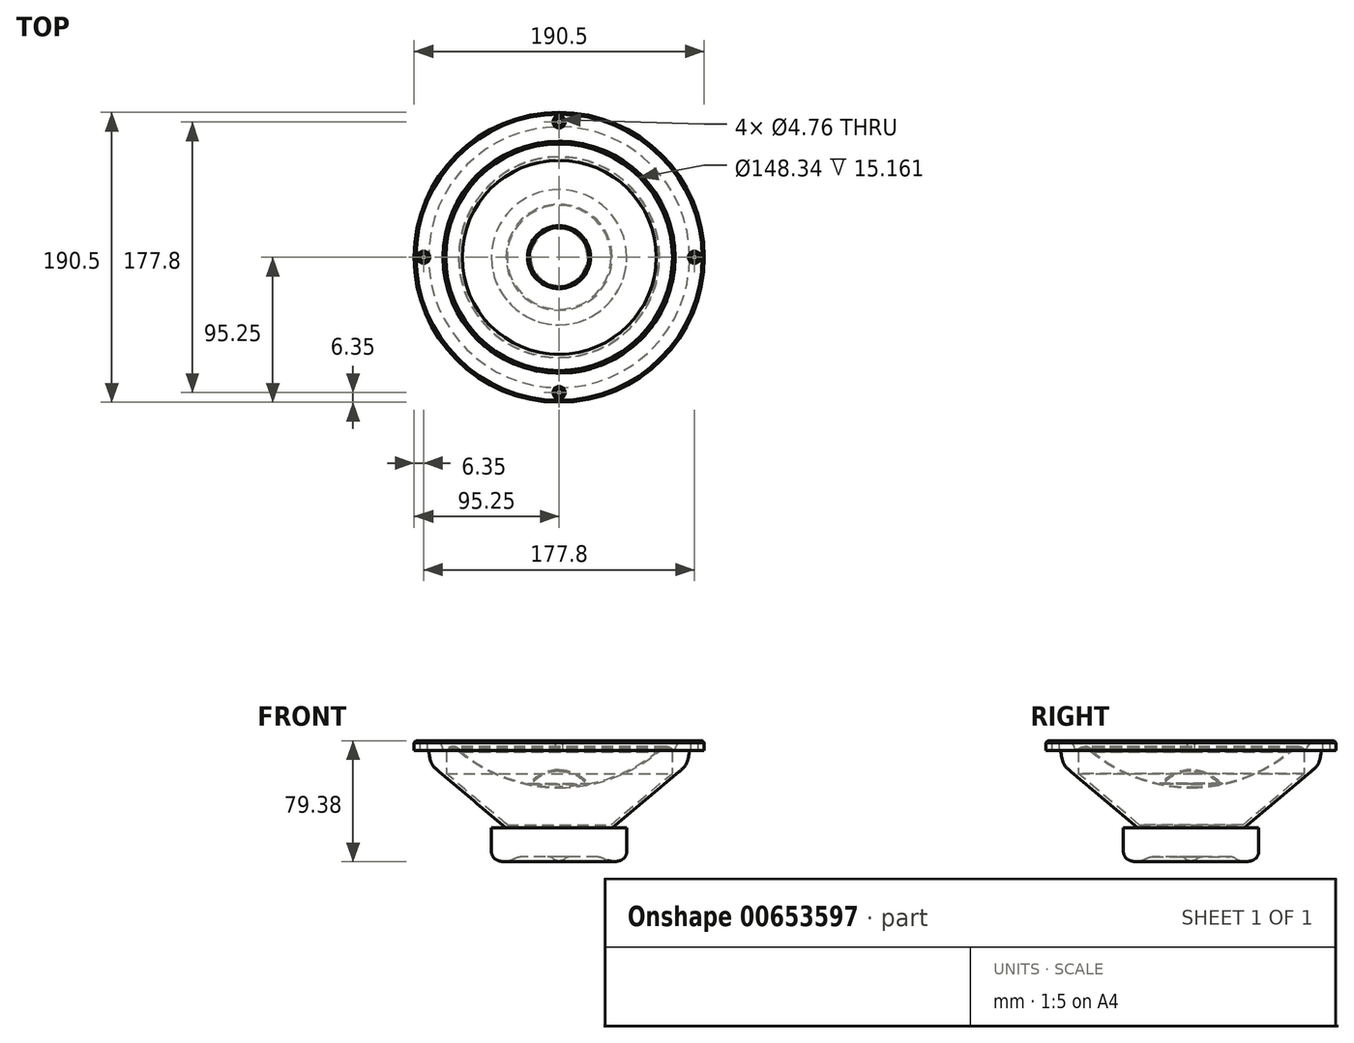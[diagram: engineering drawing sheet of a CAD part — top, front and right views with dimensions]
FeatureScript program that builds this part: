
annotation { "Feature Type Name" : "Feature", "Feature Type Description" : "" }
export const myFeature = defineFeature(function(context is Context, id is Id, definition is map)
    precondition{}
    {
        {
            var Q0;
            Q0=qCreatedBy(makeId("Front.planeOp"),FACE);
            var sketch = newSketch(context, id + "F0", { "sketchPlane" : qUnion([Q0])});
            skLineSegment(sketch, "E0", {"start": v(95.25, 76.2) * mm, "end": v(95.25, 69.85) * mm});
            skLineSegment(sketch, "E1", {"start": v(95.25, 69.85) * mm, "end": v(85.72, 69.85) * mm});
            skLineSegment(sketch, "E2", {"start": v(44.45, 19.05) * mm, "end": v(44.45, 0) * mm});
            skLineSegment(sketch, "E3", {"start": v(27.65, 0) * mm, "end": v(5.08, 0) * mm});
            skLineSegment(sketch, "E4", {"start": v(0, 0) * mm, "end": v(0, 76.2) * mm});
            skLineSegment(sketch, "E5", {"start": v(0, 0) * mm, "end": v(0, 96.52) * mm, "construction": true});
            skLineSegment(sketch, "E6", {"start": v(85.72, 69.85) * mm, "end": v(84.05, 60.33) * mm});
            skLineSegment(sketch, "E7", {"start": v(84.05, 60.33) * mm, "end": v(34.86, 19.05) * mm});
            skLineSegment(sketch, "E8", {"start": v(34.86, 19.05) * mm, "end": v(44.45, 19.05) * mm});
            skLineSegment(sketch, "E9", {"start": v(85.72, 69.85) * mm, "end": v(85.72, 49.69) * mm, "construction": true});
            skLineSegment(sketch, "E10", {"start": v(95.25, 76.2) * mm, "end": v(76.2, 76.2) * mm});
            skArc(sketch, "E11", {"start": v(19.5, 48.04) * mm, "mid": v(10.76, 54.76) * mm, "end": v(0, 57.15) * mm});
            skLineSegment(sketch, "E12", {"start": v(76.2, 76.2) * mm, "end": v(76.2, 69.85) * mm});
            skPoint(sketch, "E13.orphan", {"position": v(-19.67, 47.81) * mm});
            skArc(sketch, "E14.trimOffspring", {"start": v(19.67, 47.81) * mm, "mid": v(44.13, 55.98) * mm, "end": v(65.75, 70.03) * mm});
            skPoint(sketch, "E15.center.orphan", {"position": v(0, 148.62) * mm});
            skPoint(sketch, "E15.start.orphan", {"position": v(-65.75, 70.03) * mm});
            skArc(sketch, "E16", {"start": v(-65.75, 70.03) * mm, "mid": v(-35.02, 52.12) * mm, "end": v(0, 45.9) * mm, "construction": true});
            skArc(sketch, "E17", {"start": v(0, 57.15) * mm, "mid": v(-10.89, 54.7) * mm, "end": v(-19.67, 47.81) * mm, "construction": true});
            skArc(sketch, "E18", {"start": v(0, 45.38) * mm, "mid": v(35.2, 51.64) * mm, "end": v(66.07, 69.64) * mm});
            skArc(sketch, "E19", {"start": v(19.67, 47.81) * mm, "mid": v(9.88, 46.37) * mm, "end": v(0, 45.9) * mm});
            skArc(sketch, "E20", {"start": v(18.53, 47.6) * mm, "mid": v(10.2, 53.9) * mm, "end": v(0, 56.13) * mm});
            skArc(sketch, "E21", {"start": v(19.5, 48.04) * mm, "mid": v(20.06, 48.15) * mm, "end": v(20.64, 48.27) * mm});
            skLineSegment(sketch, "E22", {"start": v(20.64, 48.27) * mm, "end": v(20.69, 48.02) * mm});
            skLineSegment(sketch, "E23", {"start": v(34.86, 19.05) * mm, "end": v(0, 19.05) * mm});
            skLineSegment(sketch, "E24", {"start": v(74.17, 54.69) * mm, "end": v(34.12, 21.08) * mm});
            skLineSegment(sketch, "E25", {"start": v(34.12, 21.08) * mm, "end": v(0, 21.08) * mm});
            skLineSegment(sketch, "E26", {"start": v(76.2, 69.85) * mm, "end": v(74.17, 69.85) * mm});
            skLineSegment(sketch, "E27", {"start": v(74.17, 69.85) * mm, "end": v(74.17, 54.69) * mm});
            skLineSegment(sketch, "E28", {"start": v(74.46, 70.61) * mm, "end": v(76.2, 70.61) * mm});
            skLineSegment(sketch, "E29", {"start": v(65.75, 70.03) * mm, "end": v(66.07, 69.64) * mm});
            skArc(sketch, "E30", {"start": v(74.46, 70.61) * mm, "mid": v(69.85, 72.3) * mm, "end": v(65.25, 70.61) * mm});
            skArc(sketch, "E31", {"start": v(74.17, 69.85) * mm, "mid": v(70, 71.54) * mm, "end": v(65.75, 70.03) * mm});
            skArc(sketch, "E32", {"start": v(63.7, 69.31) * mm, "mid": v(64.47, 69.96) * mm, "end": v(65.25, 70.61) * mm});
            skLineSegment(sketch, "E33", {"start": v(63.7, 69.31) * mm, "end": v(64.17, 68.72) * mm});
            skArc(sketch, "E34", {"start": v(27.65, 0) * mm, "mid": v(36.05, -3.17) * mm, "end": v(44.45, 0) * mm});
            skArc(sketch, "E35", {"start": v(0, -2.54) * mm, "mid": v(2.84, -1.87) * mm, "end": v(5.08, 0) * mm});
            skLineSegment(sketch, "E36", {"start": v(0, 0) * mm, "end": v(0, -2.54) * mm});
            skSolve(sketch);
        }
        {
            var Q0;
            Q0=makeQuery(id+"F0.imprint","IMPRINT",FACE,{"disambiguationData":[TD([[makeQuery(id+"F0.imprint","IMPRINT",EDGE,{"derivedFrom":sQuery(id+"F0.wireOp",EDGE,"E0")}),-1.0]])]});
            var Q1;
            Q1=sQuery(id+"F0.wireOp",EDGE,"E5");
            revolve(context, id + "F1", {"entities" : qUnion([Q0]), "axis" : qUnion([Q1]), "revolveType" : RevolveType.FULL});
        }
        {
            var Q0;
            {var subQ0=sQuery(id+"F0.wireOp",EDGE,"E26");Q0=makeQuery(id+"F0.imprint","IMPRINT",FACE,{"disambiguationData":[TD([[makeQuery(id+"F0.imprint","IMPRINT",EDGE,{"derivedFrom":subQ0}),-1.0]])]});}
            var Q1;
            Q1=sQuery(id+"F0.wireOp",EDGE,"E5");
            revolve(context, id + "F2", {"entities" : qUnion([Q0]), "axis" : qUnion([Q1]), "revolveType" : RevolveType.FULL});
        }
        {
            var Q0;
            {var subQ0=sQuery(id+"F0.wireOp",EDGE,"E18");Q0=makeQuery(id+"F0.imprint","IMPRINT",FACE,{"disambiguationData":[TD([[makeQuery(id+"F0.imprint","IMPRINT",EDGE,{"derivedFrom":subQ0}),1.0]])]});}
            var Q1;
            Q1=sQuery(id+"F0.wireOp",EDGE,"E5");
            revolve(context, id + "F3", {"entities" : qUnion([Q0]), "axis" : qUnion([Q1]), "revolveType" : RevolveType.FULL});
        }
        {
            var Q0;
            {var subQ5=sQuery(id+"F0.wireOp",EDGE,"E11");Q0=makeQuery(id+"F0.imprint","IMPRINT",FACE,{"disambiguationData":[TD([[makeQuery(id+"F0.imprint","IMPRINT",EDGE,{"derivedFrom":subQ5}),1.0]])]});}
            var Q1;
            Q1=sQuery(id+"F0.wireOp",EDGE,"E5");
            revolve(context, id + "F4", {"entities" : qUnion([Q0]), "axis" : qUnion([Q1]), "revolveType" : RevolveType.FULL});
        }
        {
            var Q0;
            Q0=makeQuery(id+"F0.imprint","IMPRINT",FACE,{"disambiguationData":[TD([[makeQuery(id+"F0.imprint","IMPRINT",EDGE,{"derivedFrom":sQuery(id+"F0.wireOp",EDGE,"E2")}),-1.0]])]});
            var Q1;
            Q1=sQuery(id+"F0.wireOp",EDGE,"E5");
            revolve(context, id + "F5", {"entities" : qUnion([Q0]), "axis" : qUnion([Q1]), "revolveType" : RevolveType.FULL});
        }
        {
            var Q0;
            Q0=makeQuery(id+"F1.opRevolve","SWEPT_FACE",FACE,{"disambiguationData":[OSD([sQuery(id+"F0.wireOp",EDGE,"E10")])]});
            var sketch = newSketch(context, id + "F6", { "sketchPlane" : qUnion([Q0])});
            skCircle(sketch, "E37", {"center": v(0, 0) * mm, "radius": 88.9 * mm, "construction": true});
            skPoint(sketch, "E38", {"position": v(0, 88.9) * mm});
            skPoint(sketch, "E39", {"position": v(88.9, 0) * mm});
            skPoint(sketch, "E40", {"position": v(0, -88.9) * mm});
            skPoint(sketch, "E41", {"position": v(-88.9, 0) * mm});
            skSolve(sketch);
        }
        {
            var Q0;
            Q0=sQuery(id+"F6.wireOp",VERTEX,"E38");
            var Q1;
            Q1=sQuery(id+"F6.wireOp",VERTEX,"E39");
            var Q2;
            Q2=sQuery(id+"F6.wireOp",VERTEX,"E40");
            var Q3;
            Q3=sQuery(id+"F6.wireOp",VERTEX,"E41");
            var Q4;
            Q4=makeQuery(id+"F1.opRevolve","SWEPT_BODY",BODY,{"disambiguationData":[OSD([sQuery(id+"F0.wireOp",EDGE,"E0"),sQuery(id+"F0.wireOp",EDGE,"E1"),sQuery(id+"F0.wireOp",EDGE,"E2"),sQuery(id+"F0.wireOp",EDGE,"E3"),sQuery(id+"F0.wireOp",EDGE,"E4"),sQuery(id+"F0.wireOp",EDGE,"E6"),sQuery(id+"F0.wireOp",EDGE,"E7"),sQuery(id+"F0.wireOp",EDGE,"E8"),sQuery(id+"F0.wireOp",EDGE,"E10"),sQuery(id+"F0.wireOp",EDGE,"E11"),sQuery(id+"F0.wireOp",EDGE,"E12"),sQuery(id+"F0.wireOp",EDGE,"oivfGs8H-isbq-zMFm-OgCN-3ZXWerDyivmW"),sQuery(id+"F0.wireOp",EDGE,"E14.trimOffspring")])]});
            hole(context, id + "F7", {"style" : HoleStyle.C_SINK, "endStyle" : HoleEndStyle.THROUGH, "holeDiameter" : 4.76 * mm, "cSinkDiameter" : 7.94 * mm, "cSinkAngle" : 85 * degree, "majorDiameter" : 6.35 * mm, "isTappedThrough" : true, "tappedDepth" : 12.7 * mm, "tapClearance" : 3, "locations" : qUnion([Q0, Q1, Q2, Q3]), "scope" : qUnion([Q4])});
        }
        {
            var Q0;
            Q0=makeQuery(id+"F1.opRevolve","SWEPT_EDGE",EDGE,{"disambiguationData":[OSD([sQuery(id+"F0.wireOp",EDGE,"E6"),sQuery(id+"F0.wireOp",EDGE,"E7")])]});
            fillet(context, id + "F8", {"entities" : qUnion([Q0]), "radius" : 19.05 * mm, "tangentPropagation" : true, "rho" : .7, "crossSection" : FilletCrossSection.CONIC, "allowEdgeOverflow" : false});
        }
        {
            var Q0;
            Q0=makeQuery(id+"F1.opRevolve","SWEPT_EDGE",EDGE,{"disambiguationData":[OSD([sQuery(id+"F0.wireOp",EDGE,"E0"),sQuery(id+"F0.wireOp",EDGE,"E10")])]});
            chamfer(context, id + "F9", {"entities" : qUnion([Q0]), "width" : 1.27 * mm, "tangentPropagation" : true});
        }
        {
            var Q0;
            Q0=makeQuery(id+"F1.opRevolve","SWEPT_EDGE",EDGE,{"disambiguationData":[OSD([sQuery(id+"F0.wireOp",EDGE,"E10"),sQuery(id+"F0.wireOp",EDGE,"E12")])]});
            fillet(context, id + "F10", {"entities" : qUnion([Q0]), "radius" : 6.35 * mm, "tangentPropagation" : true, "rho" : .4, "crossSection" : FilletCrossSection.CONIC, "allowEdgeOverflow" : false});
        }
        {
            var Q0;
            Q0=makeQuery(id+"F5.opRevolve","SWEPT_EDGE",EDGE,{"disambiguationData":[OSD([sQuery(id+"F0.wireOp",EDGE,"E2"),sQuery(id+"F0.wireOp",EDGE,"E34")])]});
            var Q1;
            Q1=makeQuery(id+"F5.opRevolve","SWEPT_EDGE",EDGE,{"disambiguationData":[OSD([sQuery(id+"F0.wireOp",EDGE,"E3"),sQuery(id+"F0.wireOp",EDGE,"E34")])]});
            var Q2;
            Q2=makeQuery(id+"F5.opRevolve","SWEPT_EDGE",EDGE,{"disambiguationData":[OSD([sQuery(id+"F0.wireOp",EDGE,"E3"),sQuery(id+"F0.wireOp",EDGE,"E35")])]});
            fillet(context, id + "F11", {"entities" : qUnion([Q0, Q1, Q2]), "radius" : 6.35 * mm, "tangentPropagation" : true, "allowEdgeOverflow" : false});
        }
    });
